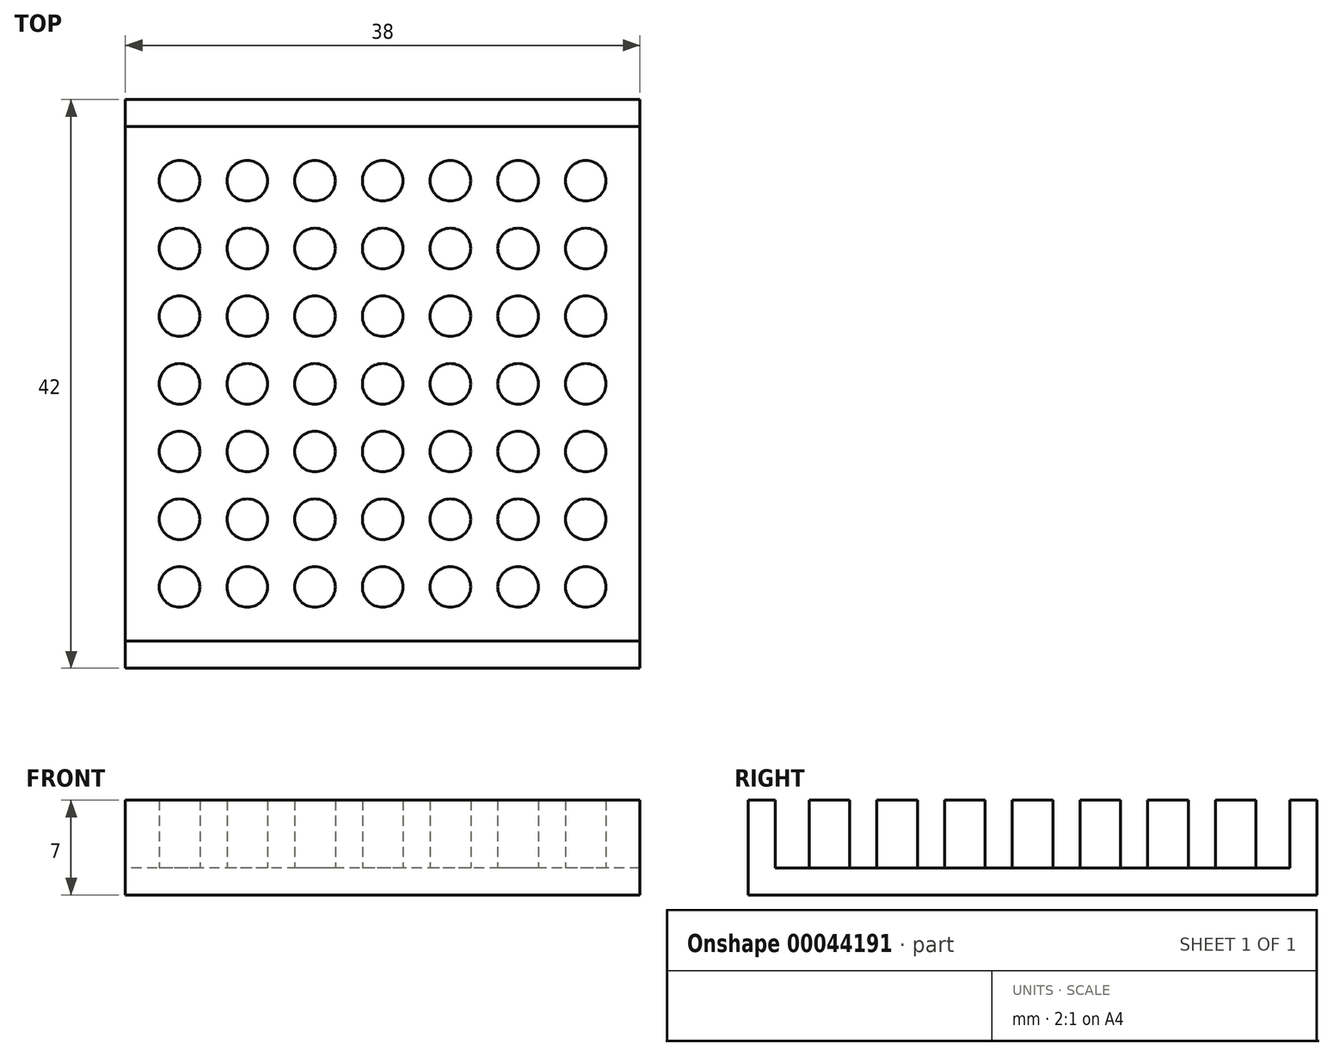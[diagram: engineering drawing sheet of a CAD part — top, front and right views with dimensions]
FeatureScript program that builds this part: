
annotation { "Feature Type Name" : "Feature", "Feature Type Description" : "" }
export const myFeature = defineFeature(function(context is Context, id is Id, definition is map)
    precondition{}
    {
        {
            var Q0;
            Q0=qCreatedBy(makeId("Top.planeOp"),FACE);
            var sketch = newSketch(context, id + "F0", { "sketchPlane" : qUnion([Q0])});
            skLineSegment(sketch, "E0.rect.bottom", {"start": v(19, 19) * mm, "end": v(-19, 19) * mm});
            skLineSegment(sketch, "E0.rect.top", {"start": v(19, -19) * mm, "end": v(-19, -19) * mm});
            skLineSegment(sketch, "E0.rect.left", {"start": v(19, 19) * mm, "end": v(19, -19) * mm});
            skLineSegment(sketch, "E0.rect.right", {"start": v(-19, 19) * mm, "end": v(-19, -19) * mm});
            skPoint(sketch, "E0.rect.middle", {"position": v(0, 0) * mm});
            skLineSegment(sketch, "E1", {"start": v(-19, 19) * mm, "end": v(-19, 21) * mm});
            skLineSegment(sketch, "E2", {"start": v(-19, 21) * mm, "end": v(19, 21) * mm});
            skLineSegment(sketch, "E3", {"start": v(19, 21) * mm, "end": v(19, 19) * mm});
            skLineSegment(sketch, "E4", {"start": v(-19, -19) * mm, "end": v(-19, -21) * mm});
            skLineSegment(sketch, "E5", {"start": v(-19, -21) * mm, "end": v(19, -21) * mm});
            skLineSegment(sketch, "E6", {"start": v(19, -21) * mm, "end": v(19, -19) * mm});
            skSolve(sketch);
        }
        {
            var Q0;
            Q0 = qSketchRegion(id + "F0", true);
            extrude(context, id + "F1", {"entities" : qUnion([Q0]), "oppositeDirection" : true, "depth" : 2 * mm});
        }
        {
            var Q0;
            Q0=makeQuery(id+"F0.imprint","IMPRINT",FACE,{"disambiguationData":[TD([[makeQuery(id+"F0.imprint","IMPRINT",EDGE,{"derivedFrom":sQuery(id+"F0.wireOp",EDGE,"E0.rect.bottom")}),1.0]])]});
            var sketch = newSketch(context, id + "F2", { "sketchPlane" : qUnion([Q0])});
            skCircle(sketch, "E7", {"center": v(0, 0) * mm, "radius": 1.5 * mm});
            skCircle(sketch, "E8.0.1.0", {"center": v(0, 5) * mm, "radius": 1.5 * mm});
            skCircle(sketch, "E8.0.2.0", {"center": v(0, 10) * mm, "radius": 1.5 * mm});
            skCircle(sketch, "E8.0.3.0", {"center": v(0, 15) * mm, "radius": 1.5 * mm});
            skCircle(sketch, "E8.1.0.0", {"center": v(5, 0) * mm, "radius": 1.5 * mm});
            skCircle(sketch, "E8.1.1.0", {"center": v(5, 5) * mm, "radius": 1.5 * mm});
            skCircle(sketch, "E8.1.2.0", {"center": v(5, 10) * mm, "radius": 1.5 * mm});
            skCircle(sketch, "E8.1.3.0", {"center": v(5, 15) * mm, "radius": 1.5 * mm});
            skCircle(sketch, "E8.2.0.0", {"center": v(10, 0) * mm, "radius": 1.5 * mm});
            skCircle(sketch, "E8.2.1.0", {"center": v(10, 5) * mm, "radius": 1.5 * mm});
            skCircle(sketch, "E8.2.2.0", {"center": v(10, 10) * mm, "radius": 1.5 * mm});
            skCircle(sketch, "E8.2.3.0", {"center": v(10, 15) * mm, "radius": 1.5 * mm});
            skCircle(sketch, "E8.3.0.0", {"center": v(15, 0) * mm, "radius": 1.5 * mm});
            skCircle(sketch, "E8.3.1.0", {"center": v(15, 5) * mm, "radius": 1.5 * mm});
            skCircle(sketch, "E8.3.2.0", {"center": v(15, 10) * mm, "radius": 1.5 * mm});
            skCircle(sketch, "E8.3.3.0", {"center": v(15, 15) * mm, "radius": 1.5 * mm});
            skLineSegment(sketch, "E8.direction1", {"start": v(0, 0) * mm, "end": v(5, 0) * mm, "construction": true});
            skLineSegment(sketch, "E8.direction2", {"start": v(0, 0) * mm, "end": v(0, 5) * mm, "construction": true});
            skCircle(sketch, "E9.1.0.6", {"center": v(-5, 0) * mm, "radius": 1.5 * mm});
            skCircle(sketch, "E9.1.0.7", {"center": v(-5, 10) * mm, "radius": 1.5 * mm});
            skCircle(sketch, "E9.1.0.10", {"center": v(-5, 5) * mm, "radius": 1.5 * mm});
            skCircle(sketch, "E9.1.0.11", {"center": v(-5, 15) * mm, "radius": 1.5 * mm});
            skCircle(sketch, "E9.2.0.0", {"center": v(-10, 10) * mm, "radius": 1.5 * mm});
            skCircle(sketch, "E9.2.0.1", {"center": v(-10, 15) * mm, "radius": 1.5 * mm});
            skCircle(sketch, "E9.2.0.2", {"center": v(-5, 10) * mm, "radius": 1.5 * mm});
            skCircle(sketch, "E9.2.0.3", {"center": v(-5, 15) * mm, "radius": 1.5 * mm});
            skCircle(sketch, "E9.2.0.4", {"center": v(-5, 0) * mm, "radius": 1.5 * mm});
            skCircle(sketch, "E9.2.0.5", {"center": v(-5, 5) * mm, "radius": 1.5 * mm});
            skCircle(sketch, "E9.2.0.6", {"center": v(-15, 0) * mm, "radius": 1.5 * mm});
            skCircle(sketch, "E9.2.0.7", {"center": v(-15, 10) * mm, "radius": 1.5 * mm});
            skCircle(sketch, "E9.2.0.8", {"center": v(-10, 0) * mm, "radius": 1.5 * mm});
            skCircle(sketch, "E9.2.0.9", {"center": v(-10, 5) * mm, "radius": 1.5 * mm});
            skCircle(sketch, "E9.2.0.10", {"center": v(-15, 5) * mm, "radius": 1.5 * mm});
            skCircle(sketch, "E9.2.0.11", {"center": v(-15, 15) * mm, "radius": 1.5 * mm});
            skLineSegment(sketch, "E9.direction1", {"start": v(10, 10) * mm, "end": v(0, 10) * mm, "construction": true});
            skLineSegment(sketch, "E10.0.1.0", {"start": v(10, -10) * mm, "end": v(0, -10) * mm, "construction": true});
            skCircle(sketch, "E10.0.1.1", {"center": v(15, -5) * mm, "radius": 1.5 * mm});
            skCircle(sketch, "E10.0.1.2", {"center": v(5, -10) * mm, "radius": 1.5 * mm});
            skCircle(sketch, "E10.0.1.3", {"center": v(0, -10) * mm, "radius": 1.5 * mm});
            skCircle(sketch, "E10.0.1.4", {"center": v(-10, -15) * mm, "radius": 1.5 * mm});
            skCircle(sketch, "E10.0.1.5", {"center": v(10, -10) * mm, "radius": 1.5 * mm});
            skCircle(sketch, "E10.0.1.6", {"center": v(-5, -10) * mm, "radius": 1.5 * mm});
            skCircle(sketch, "E10.0.1.7", {"center": v(0, -15) * mm, "radius": 1.5 * mm});
            skCircle(sketch, "E10.0.1.8", {"center": v(-5, -5) * mm, "radius": 1.5 * mm});
            skCircle(sketch, "E10.0.1.9", {"center": v(-15, -10) * mm, "radius": 1.5 * mm});
            skCircle(sketch, "E10.0.1.10", {"center": v(-10, -5) * mm, "radius": 1.5 * mm});
            skCircle(sketch, "E10.0.1.11", {"center": v(-5, -15) * mm, "radius": 1.5 * mm});
            skCircle(sketch, "E10.0.1.12", {"center": v(15, -15) * mm, "radius": 1.5 * mm});
            skLineSegment(sketch, "E10.0.1.13", {"start": v(0, -20) * mm, "end": v(0, -15) * mm, "construction": true});
            skCircle(sketch, "E10.0.1.14", {"center": v(15, -10) * mm, "radius": 1.5 * mm});
            skCircle(sketch, "E10.0.1.15", {"center": v(10, -15) * mm, "radius": 1.5 * mm});
            skCircle(sketch, "E10.0.1.16", {"center": v(5, -5) * mm, "radius": 1.5 * mm});
            skCircle(sketch, "E10.0.1.17", {"center": v(-10, -10) * mm, "radius": 1.5 * mm});
            skCircle(sketch, "E10.0.1.18", {"center": v(0, -5) * mm, "radius": 1.5 * mm});
            skCircle(sketch, "E10.0.1.19", {"center": v(-15, -15) * mm, "radius": 1.5 * mm});
            skCircle(sketch, "E10.0.1.20", {"center": v(-15, -5) * mm, "radius": 1.5 * mm});
            skCircle(sketch, "E10.0.1.21", {"center": v(5, -15) * mm, "radius": 1.5 * mm});
            skCircle(sketch, "E10.0.1.22", {"center": v(10, -5) * mm, "radius": 1.5 * mm});
            skCircle(sketch, "E10.0.1.23", {"center": v(-5, -15) * mm, "radius": 1.5 * mm});
            skCircle(sketch, "E10.0.1.24", {"center": v(0, -15) * mm, "radius": 1.5 * mm});
            skCircle(sketch, "E10.0.1.25", {"center": v(-5, -5) * mm, "radius": 1.5 * mm});
            skCircle(sketch, "E10.0.1.26", {"center": v(-5, -10) * mm, "radius": 1.5 * mm});
            skCircle(sketch, "E10.0.1.27", {"center": v(5, -10) * mm, "radius": 1.5 * mm});
            skCircle(sketch, "E10.0.1.28", {"center": v(0, -10) * mm, "radius": 1.5 * mm});
            skCircle(sketch, "E10.0.1.29", {"center": v(5, -15) * mm, "radius": 1.5 * mm});
            skCircle(sketch, "E10.0.1.30", {"center": v(5, -5) * mm, "radius": 1.5 * mm});
            skCircle(sketch, "E10.0.1.31", {"center": v(0, -5) * mm, "radius": 1.5 * mm});
            skLineSegment(sketch, "E10.direction1", {"start": v(0, 10) * mm, "end": v(25.4, 10) * mm, "construction": true});
            skLineSegment(sketch, "E10.direction2", {"start": v(0, 10) * mm, "end": v(0, -10) * mm, "construction": true});
            skSolve(sketch);
        }
        {
            var Q0;
            Q0 = qSketchRegion(id + "F2", true);
            var Q1;
            Q1=makeQuery(id+"F0.imprint","IMPRINT",FACE,{"disambiguationData":[TD([[makeQuery(id+"F0.imprint","IMPRINT",EDGE,{"derivedFrom":sQuery(id+"F0.wireOp",EDGE,"E0.rect.bottom")}),-1.0]])]});
            var Q2;
            Q2=makeQuery(id+"F0.imprint","IMPRINT",FACE,{"disambiguationData":[TD([[makeQuery(id+"F0.imprint","IMPRINT",EDGE,{"derivedFrom":sQuery(id+"F0.wireOp",EDGE,"E0.rect.top")}),1.0]])]});
            extrude(context, id + "F3", {"entities" : qUnion([Q0, Q1, Q2]), "operationType" : NewBodyOperationType.ADD, "depth" : 5 * mm});
        }
    });
